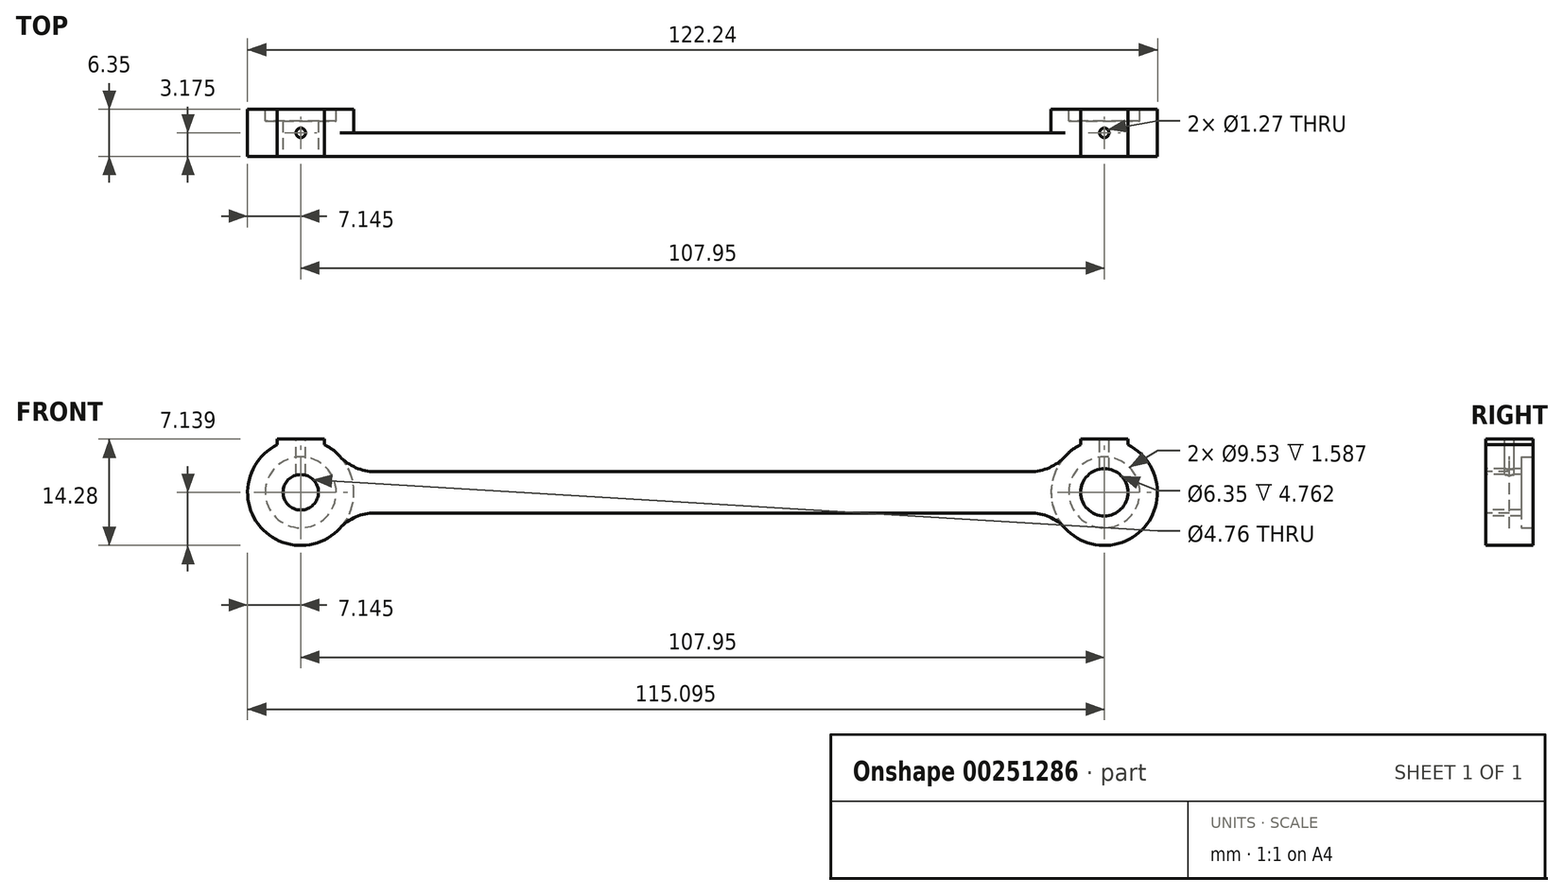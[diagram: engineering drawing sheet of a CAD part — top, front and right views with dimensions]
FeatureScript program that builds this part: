
annotation { "Feature Type Name" : "Feature", "Feature Type Description" : "" }
export const myFeature = defineFeature(function(context is Context, id is Id, definition is map)
    precondition{}
    {
        {
            var Q0;
            Q0=qCreatedBy(makeId("Front.planeOp"),FACE);
            var sketch = newSketch(context, id + "F0", { "sketchPlane" : qUnion([Q0])});
            skLineSegment(sketch, "E0", {"start": v(3.78, 14.91) * mm, "end": v(111.73, 14.91) * mm});
            skLineSegment(sketch, "E1", {"start": v(111.73, 14.91) * mm, "end": v(111.73, 20.47) * mm});
            skLineSegment(sketch, "E2", {"start": v(111.73, 20.47) * mm, "end": v(3.78, 20.47) * mm});
            skLineSegment(sketch, "E3", {"start": v(3.78, 20.47) * mm, "end": v(3.78, 14.91) * mm});
            skSolve(sketch);
        }
        {
            var Q0;
            Q0=qSketchRegion(id+"F0",true);
            extrude(context, id + "F1", {"entities" : qUnion([Q0]), "depth" : 3.17 * mm});
        }
        {
            var Q0;
            Q0=makeQuery(id+"F1.opExtrude","CAP_FACE",FACE,{"disambiguationData":[OSD([sQuery(id+"F0.wireOp",EDGE,"E0"),sQuery(id+"F0.wireOp",EDGE,"E1"),sQuery(id+"F0.wireOp",EDGE,"E2"),sQuery(id+"F0.wireOp",EDGE,"E3")])],"isStart":false});
            var sketch = newSketch(context, id + "F2", { "sketchPlane" : qUnion([Q0])});
            skCircle(sketch, "E4", {"center": v(3.78, 17.69) * mm, "radius": 7.14 * mm});
            skSolve(sketch);
        }
        {
            var Q0;
            Q0=qSketchRegion(id+"F2",true);
            extrude(context, id + "F3", {"entities" : qUnion([Q0]), "operationType" : NewBodyOperationType.ADD, "oppositeDirection" : true, "depth" : 3.17 * mm});
        }
        {
            var Q0;
            Q0=makeQuery(id+"F3.boolean.opBoolean","MERGE",FACE,{"derivedFrom":[makeQuery(id+"F1.opExtrude","CAP_FACE",FACE,{"disambiguationData":[OSD([sQuery(id+"F0.wireOp",EDGE,"E0"),sQuery(id+"F0.wireOp",EDGE,"E1"),sQuery(id+"F0.wireOp",EDGE,"E2"),sQuery(id+"F0.wireOp",EDGE,"E3")])],"isStart":false}),makeQuery(id+"F3.opExtrude","CAP_FACE",FACE,{"disambiguationData":[OSD([sQuery(id+"F2.wireOp",EDGE,"E4")])],"isStart":true})]});
            var sketch = newSketch(context, id + "F4", { "sketchPlane" : qUnion([Q0])});
            skCircle(sketch, "E5", {"center": v(3.78, 17.69) * mm, "radius": 7.14 * mm});
            skSolve(sketch);
        }
        {
            var Q0;
            Q0=qSketchRegion(id+"F4",true);
            extrude(context, id + "F5", {"entities" : qUnion([Q0]), "operationType" : NewBodyOperationType.ADD, "depth" : 3.17 * mm});
        }
        {
            var Q0;
            Q0=makeQuery(id+"F5.opExtrude","CAP_FACE",FACE,{"disambiguationData":[OSD([sQuery(id+"F4.wireOp",EDGE,"E5")])],"isStart":false});
            var sketch = newSketch(context, id + "F6", { "sketchPlane" : qUnion([Q0])});
            skCircle(sketch, "E6", {"center": v(3.78, 17.69) * mm, "radius": 2.38 * mm});
            skSolve(sketch);
        }
        {
            var Q0;
            Q0=qSketchRegion(id+"F6",true);
            extrude(context, id + "F7", {"entities" : qUnion([Q0]), "operationType" : NewBodyOperationType.REMOVE, "oppositeDirection" : true, "depth" : 25.4 * mm});
        }
        {
            var Q0;
            Q0=makeQuery(id+"F5.opExtrude","CAP_FACE",FACE,{"disambiguationData":[OSD([sQuery(id+"F4.wireOp",EDGE,"E5")])],"isStart":false});
            var sketch = newSketch(context, id + "F8", { "sketchPlane" : qUnion([Q0])});
            skLineSegment(sketch, "E7", {"start": v(-3.24, 24.83) * mm, "end": v(11.05, 24.83) * mm});
            skLineSegment(sketch, "E8", {"start": v(0.6, 24.83) * mm, "end": v(0.6, 24.09) * mm});
            skLineSegment(sketch, "E9", {"start": v(3.78, 17.69) * mm, "end": v(3.78, 24.83) * mm});
            skLineSegment(sketch, "E10", {"start": v(6.96, 24.83) * mm, "end": v(6.96, 24.09) * mm});
            skArc(sketch, "E11", {"start": v(0.6, 24.09) * mm, "mid": v(3.78, 24.83) * mm, "end": v(6.96, 24.09) * mm});
            skSolve(sketch);
        }
        {
            var Q0;
            Q0=qSketchRegion(id+"F8",true);
            extrude(context, id + "F9", {"entities" : qUnion([Q0]), "oppositeDirection" : true, "depth" : 6.35 * mm});
        }
        {
            var Q0;
            {var subQ0=sQuery(id+"F8.wireOp",EDGE,"E7");Q0=makeQuery(id+"F9.opExtrude","SWEPT_FACE",FACE,{"disambiguationData":[OSD([subQ0]),TDD([makeQuery(id+"F8.imprint","IMPRINT",EDGE,{"disambiguationData":[TD([[makeQuery(id+"F8.imprint","INTERSECT",VERTEX,{"derivedFrom":[subQ0,sQuery(id+"F8.wireOp",EDGE,"E8")]}),-1.0]])],"derivedFrom":subQ0})])]});}
            var sketch = newSketch(context, id + "F10", { "sketchPlane" : qUnion([Q0])});
            skCircle(sketch, "E12", {"center": v(3.78, -3.17) * mm, "radius": 0.64 * mm});
            skSolve(sketch);
        }
        {
            var Q0;
            Q0=makeQuery(id+"F1.opExtrude","SWEPT_BODY",BODY,{"disambiguationData":[OSD([sQuery(id+"F0.wireOp",EDGE,"E0"),sQuery(id+"F0.wireOp",EDGE,"E1"),sQuery(id+"F0.wireOp",EDGE,"E2"),sQuery(id+"F0.wireOp",EDGE,"E3")])]});
            var Q1;
            Q1=makeQuery(id+"F9.opExtrude","SWEPT_BODY",BODY,{"disambiguationData":[OSD([sQuery(id+"F8.wireOp",EDGE,"E7"),sQuery(id+"F8.wireOp",EDGE,"E8"),sQuery(id+"F8.wireOp",EDGE,"E11")])]});
            var Q2;
            Q2=makeQuery(id+"F9.opExtrude","SWEPT_BODY",BODY,{"disambiguationData":[OSD([sQuery(id+"F8.wireOp",EDGE,"E7"),sQuery(id+"F8.wireOp",EDGE,"E10"),sQuery(id+"F8.wireOp",EDGE,"E11")])]});
            booleanBodies(context, id + "F11", {"operationType" : BooleanOperationType.UNION, "tools" : qUnion([Q0, Q1, Q2])});
        }
        {
            var Q0;
            {var subQ0=sQuery(id+"F10.wireOp",EDGE,"E12");var subQ1=sQuery(id+"F8.wireOp",EDGE,"E11");var subQ2=sQuery(id+"F8.wireOp",EDGE,"E7");var subQ3=makeQuery(id+"F9.opExtrude","SWEPT_EDGE",EDGE,{"disambiguationData":[OSD([subQ2,subQ1]),ownerDisambiguation([makeQuery(id+"F9.opExtrude","SWEPT_BODY",BODY,{"disambiguationData":[OSD([subQ2,sQuery(id+"F8.wireOp",EDGE,"E8"),subQ1])]})])]});var subQ4=makeQuery(id+"F10.imprint","INTERSECT",VERTEX,{"disambiguationData":[OD(0.0)],"derivedFrom":[subQ3,subQ0]});Q0=makeQuery(id+"F10.imprint","IMPRINT",FACE,{"disambiguationData":[TD([[makeQuery(id+"F10.imprint","IMPRINT",EDGE,{"disambiguationData":[TD([[subQ4,1.0]])],"derivedFrom":subQ0}),1.0]])]});}
            var Q1;
            {var subQ0=sQuery(id+"F10.wireOp",EDGE,"E12");var subQ1=sQuery(id+"F8.wireOp",EDGE,"E11");var subQ2=sQuery(id+"F8.wireOp",EDGE,"E7");var subQ3=makeQuery(id+"F9.opExtrude","SWEPT_EDGE",EDGE,{"disambiguationData":[OSD([subQ2,subQ1]),ownerDisambiguation([makeQuery(id+"F9.opExtrude","SWEPT_BODY",BODY,{"disambiguationData":[OSD([subQ2,sQuery(id+"F8.wireOp",EDGE,"E8"),subQ1])]})])]});var subQ4=makeQuery(id+"F10.imprint","INTERSECT",VERTEX,{"disambiguationData":[OD(0.0)],"derivedFrom":[subQ3,subQ0]});Q1=makeQuery(id+"F10.imprint","IMPRINT",FACE,{"disambiguationData":[TD([[makeQuery(id+"F10.imprint","IMPRINT",EDGE,{"disambiguationData":[TD([[subQ4,-1.0]])],"derivedFrom":subQ0}),1.0]])]});}
            extrude(context, id + "F12", {"entities" : qUnion([Q0, Q1]), "operationType" : NewBodyOperationType.REMOVE, "oppositeDirection" : true, "depth" : 6.35 * mm});
        }
        {
            var Q0;
            Q0=makeQuery(id+"F3.boolean.opBoolean","MERGE",FACE,{"derivedFrom":[makeQuery(id+"F1.opExtrude","CAP_FACE",FACE,{"disambiguationData":[OSD([sQuery(id+"F0.wireOp",EDGE,"E0"),sQuery(id+"F0.wireOp",EDGE,"E1"),sQuery(id+"F0.wireOp",EDGE,"E2"),sQuery(id+"F0.wireOp",EDGE,"E3")])],"isStart":false}),makeQuery(id+"F3.opExtrude","CAP_FACE",FACE,{"disambiguationData":[OSD([sQuery(id+"F2.wireOp",EDGE,"E4")])],"isStart":true})]});
            var sketch = newSketch(context, id + "F13", { "sketchPlane" : qUnion([Q0])});
            skCircle(sketch, "E13", {"center": v(111.73, 17.69) * mm, "radius": 7.14 * mm});
            skSolve(sketch);
        }
        {
            var Q0;
            Q0=qSketchRegion(id+"F13",true);
            extrude(context, id + "F14", {"entities" : qUnion([Q0]), "operationType" : NewBodyOperationType.ADD, "oppositeDirection" : true, "depth" : 3.17 * mm});
        }
        {
            var Q0;
            Q0=makeQuery(id+"F14.boolean.opBoolean","MERGE",FACE,{"derivedFrom":[makeQuery(id+"F3.boolean.opBoolean","MERGE",FACE,{"derivedFrom":[makeQuery(id+"F1.opExtrude","CAP_FACE",FACE,{"disambiguationData":[OSD([sQuery(id+"F0.wireOp",EDGE,"E0"),sQuery(id+"F0.wireOp",EDGE,"E1"),sQuery(id+"F0.wireOp",EDGE,"E2"),sQuery(id+"F0.wireOp",EDGE,"E3")])],"isStart":false}),makeQuery(id+"F3.opExtrude","CAP_FACE",FACE,{"disambiguationData":[OSD([sQuery(id+"F2.wireOp",EDGE,"E4")])],"isStart":true})]}),makeQuery(id+"F14.opExtrude","CAP_FACE",FACE,{"disambiguationData":[OSD([sQuery(id+"F13.wireOp",EDGE,"E13")])],"isStart":true})]});
            var sketch = newSketch(context, id + "F15", { "sketchPlane" : qUnion([Q0])});
            skCircle(sketch, "E14", {"center": v(111.73, 17.69) * mm, "radius": 7.14 * mm});
            skSolve(sketch);
        }
        {
            var Q0;
            Q0=qSketchRegion(id+"F15",true);
            extrude(context, id + "F16", {"entities" : qUnion([Q0]), "operationType" : NewBodyOperationType.ADD, "depth" : 3.17 * mm});
        }
        {
            var Q0;
            Q0=makeQuery(id+"F16.opExtrude","CAP_FACE",FACE,{"disambiguationData":[OSD([sQuery(id+"F15.wireOp",EDGE,"E14")])],"isStart":false});
            var sketch = newSketch(context, id + "F17", { "sketchPlane" : qUnion([Q0])});
            skCircle(sketch, "E15", {"center": v(111.73, 17.69) * mm, "radius": 3.18 * mm});
            skSolve(sketch);
        }
        {
            var Q0;
            Q0=qSketchRegion(id+"F17",true);
            extrude(context, id + "F18", {"entities" : qUnion([Q0]), "operationType" : NewBodyOperationType.REMOVE, "oppositeDirection" : true, "depth" : 25.4 * mm});
        }
        {
            var Q0;
            Q0=makeQuery(id+"F16.opExtrude","CAP_FACE",FACE,{"disambiguationData":[OSD([sQuery(id+"F15.wireOp",EDGE,"E14")])],"isStart":false});
            var sketch = newSketch(context, id + "F19", { "sketchPlane" : qUnion([Q0])});
            skLineSegment(sketch, "E16", {"start": v(103.62, 24.83) * mm, "end": v(118.22, 24.83) * mm});
            skLineSegment(sketch, "E17", {"start": v(108.56, 24.83) * mm, "end": v(108.56, 24.09) * mm});
            skLineSegment(sketch, "E18", {"start": v(114.9, 24.83) * mm, "end": v(114.9, 24.09) * mm});
            skLineSegment(sketch, "E19", {"start": v(111.73, 17.69) * mm, "end": v(111.73, 24.83) * mm});
            skArc(sketch, "E20", {"start": v(108.56, 24.09) * mm, "mid": v(111.73, 24.83) * mm, "end": v(114.9, 24.09) * mm});
            skSolve(sketch);
        }
        {
            var Q0;
            Q0=qSketchRegion(id+"F19",true);
            extrude(context, id + "F20", {"entities" : qUnion([Q0]), "operationType" : NewBodyOperationType.ADD, "oppositeDirection" : true, "depth" : 6.35 * mm});
        }
        {
            var Q0;
            {var subQ0=sQuery(id+"F19.wireOp",EDGE,"E16");Q0=makeQuery(id+"F20.boolean.opBoolean","MERGE",FACE,{"derivedFrom":[makeQuery(id+"F20.opExtrude","SWEPT_FACE",FACE,{"disambiguationData":[OSD([subQ0]),TDD([makeQuery(id+"F19.imprint","IMPRINT",EDGE,{"disambiguationData":[TD([[makeQuery(id+"F19.imprint","INTERSECT",VERTEX,{"derivedFrom":[subQ0,sQuery(id+"F19.wireOp",EDGE,"E17")]}),-1.0]])],"derivedFrom":subQ0})])]}),makeQuery(id+"F20.opExtrude","SWEPT_FACE",FACE,{"disambiguationData":[OSD([subQ0]),TDD([makeQuery(id+"F19.imprint","IMPRINT",EDGE,{"disambiguationData":[TD([[makeQuery(id+"F19.imprint","INTERSECT",VERTEX,{"derivedFrom":[subQ0,sQuery(id+"F19.wireOp",EDGE,"E18")]}),1.0]])],"derivedFrom":subQ0})])]})]});}
            var sketch = newSketch(context, id + "F21", { "sketchPlane" : qUnion([Q0])});
            skCircle(sketch, "E21", {"center": v(111.73, -3.18) * mm, "radius": 0.64 * mm});
            skSolve(sketch);
        }
        {
            var Q0;
            Q0=qSketchRegion(id+"F21",true);
            extrude(context, id + "F22", {"entities" : qUnion([Q0]), "operationType" : NewBodyOperationType.REMOVE, "oppositeDirection" : true, "depth" : 6.35 * mm});
        }
        {
            var Q0;
            Q0=makeQuery(id+"F3.boolean.opBoolean","INTERSECT",EDGE,{"derivedFrom":[makeQuery(id+"F1.opExtrude","SWEPT_FACE",FACE,{"disambiguationData":[OSD([sQuery(id+"F0.wireOp",EDGE,"E2")])]}),makeQuery(id+"F3.opExtrude","SWEPT_FACE",FACE,{"disambiguationData":[OSD([sQuery(id+"F2.wireOp",EDGE,"E4")])]})]});
            var Q1;
            Q1=makeQuery(id+"F3.boolean.opBoolean","INTERSECT",EDGE,{"derivedFrom":[makeQuery(id+"F1.opExtrude","SWEPT_FACE",FACE,{"disambiguationData":[OSD([sQuery(id+"F0.wireOp",EDGE,"E0")])]}),makeQuery(id+"F3.opExtrude","SWEPT_FACE",FACE,{"disambiguationData":[OSD([sQuery(id+"F2.wireOp",EDGE,"E4")])]})]});
            var Q2;
            Q2=makeQuery(id+"F14.boolean.opBoolean","INTERSECT",EDGE,{"derivedFrom":[makeQuery(id+"F1.opExtrude","SWEPT_FACE",FACE,{"disambiguationData":[OSD([sQuery(id+"F0.wireOp",EDGE,"E2")])]}),makeQuery(id+"F14.opExtrude","SWEPT_FACE",FACE,{"disambiguationData":[OSD([sQuery(id+"F13.wireOp",EDGE,"E13")])]})]});
            var Q3;
            Q3=makeQuery(id+"F14.boolean.opBoolean","INTERSECT",EDGE,{"derivedFrom":[makeQuery(id+"F1.opExtrude","SWEPT_FACE",FACE,{"disambiguationData":[OSD([sQuery(id+"F0.wireOp",EDGE,"E0")])]}),makeQuery(id+"F14.opExtrude","SWEPT_FACE",FACE,{"disambiguationData":[OSD([sQuery(id+"F13.wireOp",EDGE,"E13")])]})]});
            var Q4;
            Q4=makeQuery(id+"F9.opExtrude","SWEPT_EDGE",EDGE,{"disambiguationData":[OSD([sQuery(id+"F4.wireOp",EDGE,"E5"),sQuery(id+"F8.wireOp",EDGE,"E10"),sQuery(id+"F8.wireOp",EDGE,"E11")])]});
            var Q5;
            Q5=makeQuery(id+"F9.opExtrude","SWEPT_EDGE",EDGE,{"disambiguationData":[OSD([sQuery(id+"F4.wireOp",EDGE,"E5"),sQuery(id+"F8.wireOp",EDGE,"E8"),sQuery(id+"F8.wireOp",EDGE,"E11")])]});
            var Q6;
            Q6=makeQuery(id+"F20.opExtrude","SWEPT_EDGE",EDGE,{"disambiguationData":[OSD([sQuery(id+"F15.wireOp",EDGE,"E14"),sQuery(id+"F19.wireOp",EDGE,"E17"),sQuery(id+"F19.wireOp",EDGE,"E20")])]});
            var Q7;
            Q7=makeQuery(id+"F20.opExtrude","SWEPT_EDGE",EDGE,{"disambiguationData":[OSD([sQuery(id+"F15.wireOp",EDGE,"E14"),sQuery(id+"F19.wireOp",EDGE,"E18"),sQuery(id+"F19.wireOp",EDGE,"E20")])]});
            fillet(context, id + "F23", {"entities" : qUnion([Q0, Q1, Q2, Q3, Q4, Q5, Q6, Q7]), "radius" : 6.35 * mm, "tangentPropagation" : true, "allowEdgeOverflow" : false});
        }
        {
            var Q0;
            Q0=makeQuery(id+"F14.boolean.opBoolean","MERGE",FACE,{"derivedFrom":[makeQuery(id+"F3.boolean.opBoolean","MERGE",FACE,{"derivedFrom":[makeQuery(id+"F1.opExtrude","CAP_FACE",FACE,{"disambiguationData":[OSD([sQuery(id+"F0.wireOp",EDGE,"E0"),sQuery(id+"F0.wireOp",EDGE,"E1"),sQuery(id+"F0.wireOp",EDGE,"E2"),sQuery(id+"F0.wireOp",EDGE,"E3")])],"isStart":false}),makeQuery(id+"F3.opExtrude","CAP_FACE",FACE,{"disambiguationData":[OSD([sQuery(id+"F2.wireOp",EDGE,"E4")])],"isStart":true})]}),makeQuery(id+"F14.opExtrude","CAP_FACE",FACE,{"disambiguationData":[OSD([sQuery(id+"F13.wireOp",EDGE,"E13")])],"isStart":true})]});
            extrude(context, id + "F24", {"entities" : qUnion([Q0]), "operationType" : NewBodyOperationType.ADD, "depth" : 3.17 * mm});
        }
        {
            var Q0;
            {var subQ0=sQuery(id+"F19.wireOp",EDGE,"E20");var subQ1=sQuery(id+"F19.wireOp",EDGE,"E16");var subQ2=sQuery(id+"F8.wireOp",EDGE,"E11");var subQ3=sQuery(id+"F8.wireOp",EDGE,"E7");Q0=makeQuery(id+"F20.boolean.opBoolean","MERGE",FACE,{"derivedFrom":[makeQuery(id+"F14.boolean.opBoolean","MERGE",FACE,{"derivedFrom":[makeQuery(id+"F11.opBoolean","MERGE",FACE,{"derivedFrom":[makeQuery(id+"F3.boolean.opBoolean","MERGE",FACE,{"derivedFrom":[makeQuery(id+"F1.opExtrude","CAP_FACE",FACE,{"disambiguationData":[OSD([sQuery(id+"F0.wireOp",EDGE,"E0"),sQuery(id+"F0.wireOp",EDGE,"E1"),sQuery(id+"F0.wireOp",EDGE,"E2"),sQuery(id+"F0.wireOp",EDGE,"E3")])],"isStart":true}),makeQuery(id+"F3.opExtrude","CAP_FACE",FACE,{"disambiguationData":[OSD([sQuery(id+"F2.wireOp",EDGE,"E4")])],"isStart":false})]}),makeQuery(id+"F9.opExtrude","CAP_FACE",FACE,{"disambiguationData":[OSD([subQ3,sQuery(id+"F8.wireOp",EDGE,"E8"),subQ2])],"isStart":false}),makeQuery(id+"F9.opExtrude","CAP_FACE",FACE,{"disambiguationData":[OSD([subQ3,sQuery(id+"F8.wireOp",EDGE,"E10"),subQ2])],"isStart":false})]}),makeQuery(id+"F14.opExtrude","CAP_FACE",FACE,{"disambiguationData":[OSD([sQuery(id+"F13.wireOp",EDGE,"E13")])],"isStart":false})]}),makeQuery(id+"F20.opExtrude","CAP_FACE",FACE,{"disambiguationData":[OSD([subQ1,sQuery(id+"F19.wireOp",EDGE,"E17"),subQ0])],"isStart":false}),makeQuery(id+"F20.opExtrude","CAP_FACE",FACE,{"disambiguationData":[OSD([subQ1,sQuery(id+"F19.wireOp",EDGE,"E18"),subQ0])],"isStart":false})]});}
            var sketch = newSketch(context, id + "F25", { "sketchPlane" : qUnion([Q0])});
            skArc(sketch, "E22", {"start": v(-9.05, 12.86) * mm, "mid": v(-10.91, 18.16) * mm, "end": v(-8.37, 23.17) * mm});
            skArc(sketch, "E23", {"start": v(-107.15, 23.17) * mm, "mid": v(-104.6, 18.16) * mm, "end": v(-106.47, 12.86) * mm});
            skSolve(sketch);
        }
        {
            var Q0;
            {var subQ15=sQuery(id+"F0.wireOp",EDGE,"E0");Q0=makeQuery(id+"F25.imprint","IMPRINT",FACE,{"disambiguationData":[TD([[makeQuery(id+"F25.imprint","IMPRINT",EDGE,{"derivedFrom":makeQuery(id+"F1.opExtrude","CAP_EDGE",EDGE,{"disambiguationData":[OSD([subQ15])],"isStart":true})}),-1.0]])]});}
            extrude(context, id + "F26", {"entities" : qUnion([Q0]), "operationType" : NewBodyOperationType.REMOVE, "oppositeDirection" : true, "depth" : 3.17 * mm});
        }
        {
            var Q0;
            {var subQ0=sQuery(id+"F8.wireOp",EDGE,"E8");var subQ1=sQuery(id+"F8.wireOp",EDGE,"E7");var subQ2=sQuery(id+"F8.wireOp",EDGE,"E11");var subQ5=sQuery(id+"F8.wireOp",EDGE,"E10");var subQ6=sQuery(id+"F2.wireOp",EDGE,"E4");var subQ7=sQuery(id+"F19.wireOp",EDGE,"E20");var subQ8=sQuery(id+"F19.wireOp",EDGE,"E16");Q0=makeQuery(id+"F26.boolean.opBoolean","SPLIT",FACE,{"disambiguationData":[TD([makeQuery(id+"F3.opExtrude","SWEPT_FACE",FACE,{"disambiguationData":[OSD([subQ6])]})])],"derivedFrom":makeQuery(id+"F20.boolean.opBoolean","MERGE",FACE,{"derivedFrom":[makeQuery(id+"F14.boolean.opBoolean","MERGE",FACE,{"derivedFrom":[makeQuery(id+"F11.opBoolean","MERGE",FACE,{"derivedFrom":[makeQuery(id+"F3.boolean.opBoolean","MERGE",FACE,{"derivedFrom":[makeQuery(id+"F1.opExtrude","CAP_FACE",FACE,{"disambiguationData":[OSD([sQuery(id+"F0.wireOp",EDGE,"E0"),sQuery(id+"F0.wireOp",EDGE,"E1"),sQuery(id+"F0.wireOp",EDGE,"E2"),sQuery(id+"F0.wireOp",EDGE,"E3")])],"isStart":true}),makeQuery(id+"F3.opExtrude","CAP_FACE",FACE,{"disambiguationData":[OSD([subQ6])],"isStart":false})]}),makeQuery(id+"F9.opExtrude","CAP_FACE",FACE,{"disambiguationData":[OSD([subQ1,subQ0,subQ2])],"isStart":false}),makeQuery(id+"F9.opExtrude","CAP_FACE",FACE,{"disambiguationData":[OSD([subQ1,subQ5,subQ2])],"isStart":false})]}),makeQuery(id+"F14.opExtrude","CAP_FACE",FACE,{"disambiguationData":[OSD([sQuery(id+"F13.wireOp",EDGE,"E13")])],"isStart":false})]}),makeQuery(id+"F20.opExtrude","CAP_FACE",FACE,{"disambiguationData":[OSD([subQ8,sQuery(id+"F19.wireOp",EDGE,"E17"),subQ7])],"isStart":false}),makeQuery(id+"F20.opExtrude","CAP_FACE",FACE,{"disambiguationData":[OSD([subQ8,sQuery(id+"F19.wireOp",EDGE,"E18"),subQ7])],"isStart":false})]})});}
            var sketch = newSketch(context, id + "F27", { "sketchPlane" : qUnion([Q0])});
            skCircle(sketch, "E24", {"center": v(-3.78, 17.69) * mm, "radius": 4.76 * mm});
            skSolve(sketch);
        }
        {
            var Q0;
            Q0 = qSketchRegion(id + "F27", true);
            extrude(context, id + "F28", {"entities" : qUnion([Q0]), "operationType" : NewBodyOperationType.REMOVE, "oppositeDirection" : true, "depth" : 1.59 * mm});
        }
        {
            var Q0;
            {var subQ0=sQuery(id+"F19.wireOp",EDGE,"E17");var subQ1=sQuery(id+"F19.wireOp",EDGE,"E16");var subQ2=sQuery(id+"F19.wireOp",EDGE,"E20");var subQ5=sQuery(id+"F13.wireOp",EDGE,"E13");var subQ6=sQuery(id+"F19.wireOp",EDGE,"E18");var subQ7=sQuery(id+"F8.wireOp",EDGE,"E11");var subQ8=sQuery(id+"F8.wireOp",EDGE,"E7");Q0=makeQuery(id+"F26.boolean.opBoolean","SPLIT",FACE,{"disambiguationData":[TD([makeQuery(id+"F14.opExtrude","SWEPT_FACE",FACE,{"disambiguationData":[OSD([subQ5])]})])],"derivedFrom":makeQuery(id+"F20.boolean.opBoolean","MERGE",FACE,{"derivedFrom":[makeQuery(id+"F14.boolean.opBoolean","MERGE",FACE,{"derivedFrom":[makeQuery(id+"F11.opBoolean","MERGE",FACE,{"derivedFrom":[makeQuery(id+"F3.boolean.opBoolean","MERGE",FACE,{"derivedFrom":[makeQuery(id+"F1.opExtrude","CAP_FACE",FACE,{"disambiguationData":[OSD([sQuery(id+"F0.wireOp",EDGE,"E0"),sQuery(id+"F0.wireOp",EDGE,"E1"),sQuery(id+"F0.wireOp",EDGE,"E2"),sQuery(id+"F0.wireOp",EDGE,"E3")])],"isStart":true}),makeQuery(id+"F3.opExtrude","CAP_FACE",FACE,{"disambiguationData":[OSD([sQuery(id+"F2.wireOp",EDGE,"E4")])],"isStart":false})]}),makeQuery(id+"F9.opExtrude","CAP_FACE",FACE,{"disambiguationData":[OSD([subQ8,sQuery(id+"F8.wireOp",EDGE,"E8"),subQ7])],"isStart":false}),makeQuery(id+"F9.opExtrude","CAP_FACE",FACE,{"disambiguationData":[OSD([subQ8,sQuery(id+"F8.wireOp",EDGE,"E10"),subQ7])],"isStart":false})]}),makeQuery(id+"F14.opExtrude","CAP_FACE",FACE,{"disambiguationData":[OSD([subQ5])],"isStart":false})]}),makeQuery(id+"F20.opExtrude","CAP_FACE",FACE,{"disambiguationData":[OSD([subQ1,subQ0,subQ2])],"isStart":false}),makeQuery(id+"F20.opExtrude","CAP_FACE",FACE,{"disambiguationData":[OSD([subQ1,subQ6,subQ2])],"isStart":false})]})});}
            var sketch = newSketch(context, id + "F29", { "sketchPlane" : qUnion([Q0])});
            skCircle(sketch, "E25", {"center": v(-111.73, 17.69) * mm, "radius": 4.76 * mm});
            skSolve(sketch);
        }
        {
            var Q0;
            Q0 = qSketchRegion(id + "F29", true);
            extrude(context, id + "F30", {"entities" : qUnion([Q0]), "operationType" : NewBodyOperationType.REMOVE, "oppositeDirection" : true, "depth" : 1.59 * mm});
        }
    });
